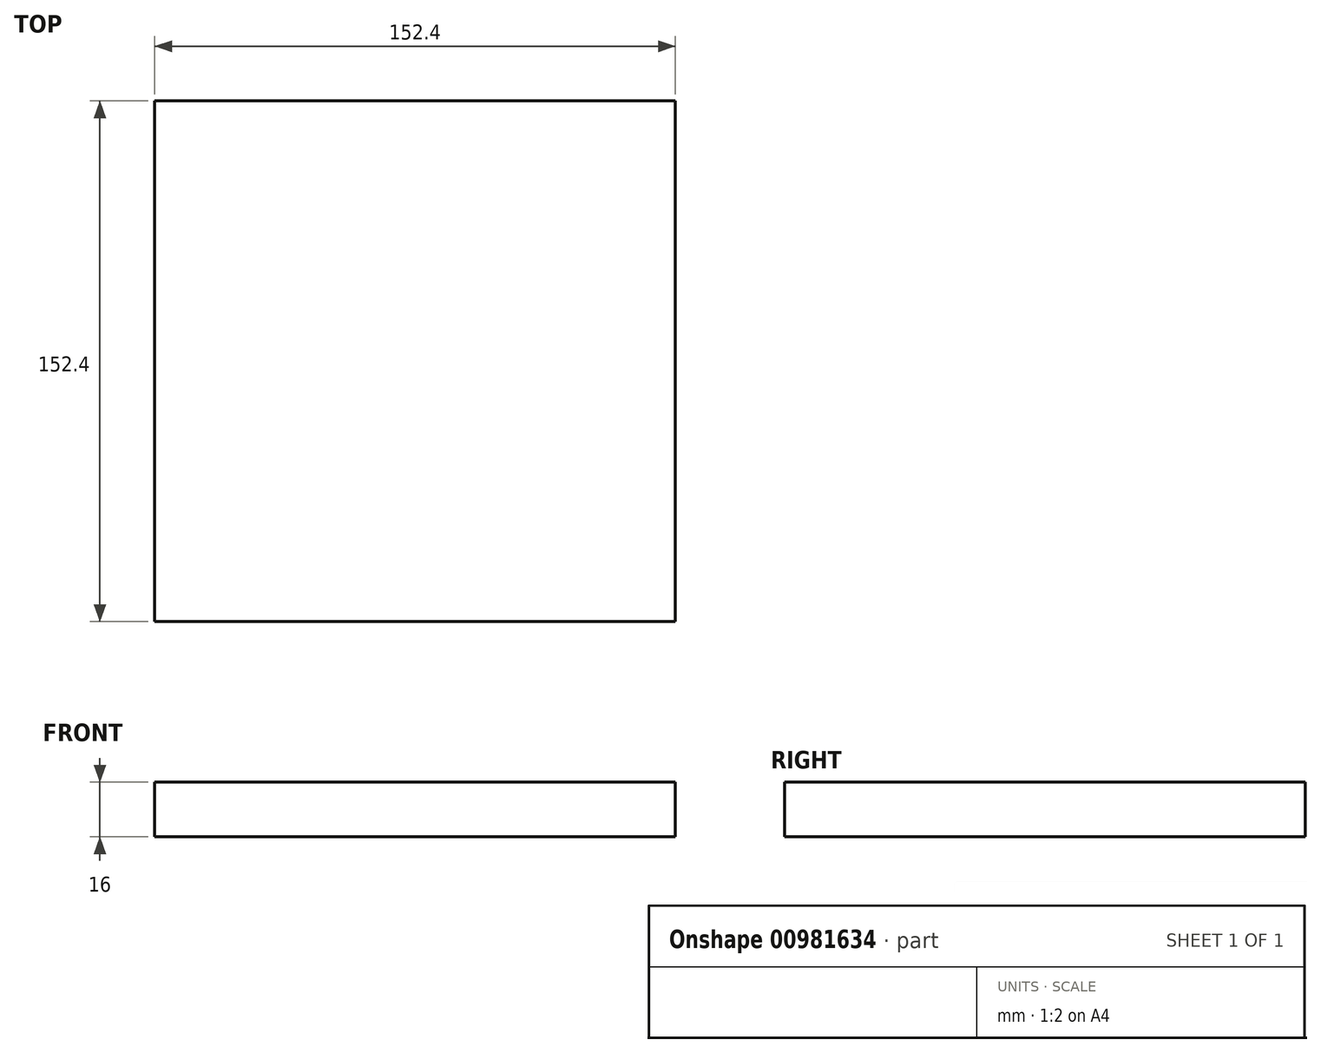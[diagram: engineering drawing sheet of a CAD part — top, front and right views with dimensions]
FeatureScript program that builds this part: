
annotation { "Feature Type Name" : "Feature", "Feature Type Description" : "" }
export const myFeature = defineFeature(function(context is Context, id is Id, definition is map)
    precondition{}
    {
        {
            var Q0;
            Q0=qCreatedBy(makeId("Top.planeOp"),FACE);
            var sketch = newSketch(context, id + "F0", { "sketchPlane" : qUnion([Q0])});
            skLineSegment(sketch, "E0.bottom", {"start": v(-117.23, 83.67) * mm, "end": v(35.17, 83.67) * mm});
            skLineSegment(sketch, "E0.top", {"start": v(-117.23, -68.73) * mm, "end": v(35.17, -68.73) * mm});
            skLineSegment(sketch, "E0.left", {"start": v(-117.23, 83.67) * mm, "end": v(-117.23, -68.73) * mm});
            skLineSegment(sketch, "E0.right", {"start": v(35.17, 83.67) * mm, "end": v(35.17, -68.73) * mm});
            skSolve(sketch);
        }
        {
            var Q0;
            Q0 = qSketchRegion(id + "F0", true);
            extrude(context, id + "F1", {"entities" : qUnion([Q0]), "depth" : 16 * mm, "offsetDistance" : 25 * mm});
        }
    });
